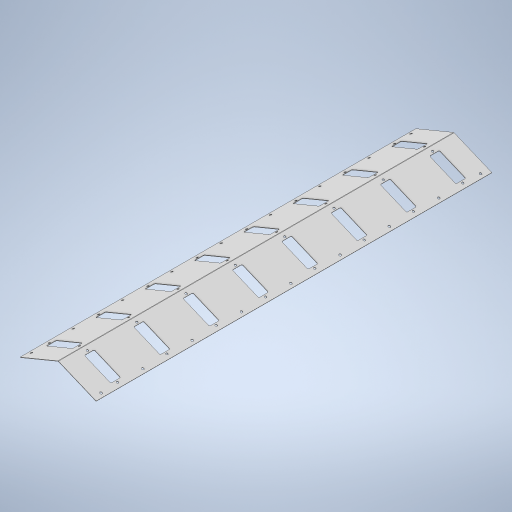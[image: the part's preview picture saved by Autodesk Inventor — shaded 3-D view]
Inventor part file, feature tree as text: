
AUTODESK INVENTOR PART (.ipt)
format: ipt  version: 2024.2 (Build 282272000, 272)  size: 656,896 bytes
history: native  units: mm
features: sketch x4, sheet_metal_op x3, extrude x3, other x3, pattern_linear x2, fillet x1, pattern_circular x1, mirror x1, chamfer x1
ambient origin geometry x8: Origin, YZ Plane, XZ Plane, XY Plane, X Axis, Y Axis, Z Axis, Center Point
bodies: Body1 (feature_tree)
feature tree (19):
  sheet_metal_op  "Contour Flange2"
  extrude  "Extrusion5"  Depth=0.9mm
  extrude  "Extrusion7"  Depth=2.0mm
  fillet  "Fillet2"  Radius=2.0mm
  pattern_circular  "Circular Pattern1"  [2 undecoded]
  pattern_linear  "Rectangular Pattern5"  Spacing1=2006.0mm  [1 undecoded]
  extrude  "Extrusion8"  Depth=2.0mm
  pattern_linear  "Rectangular Pattern6"  Spacing1=3.0mm  [1 undecoded]
  mirror  "Mirror5"
  other  "Corner Chamfer1"
  chamfer  "Corner Round1"
  sketch  "Sketch1"  dims[d46=506.0mm d47=0.9mm]
  other  "Plate4"
  sheet_metal_op  "Bend4"
  sheet_metal_op  "Corner4"
  sketch  "Sketch12"  dims[d48=4.0mm d49=2.0mm d50=2.0mm]
  sketch  "Sketch14"  dims[d51=1.0mm]
  sketch  "Sketch15"  dims[d52=4.0mm d53=2.0mm d54=2006.0mm d55=2.0mm d56=3.0mm d57=8.0mm d58=2.0mm d59=2.0mm d115=11.0mm d116=189.129mm d117=40.75mm d118=11.0mm d119=189.129mm d120=40.75mm d121=10.0mm d122=0.0mm d131=145.0mm d132=50.0mm d133=10.0mm d134=10.0mm d135=125.0mm d136=103.139mm d137=10.0mm d138=0.0mm d139=5.0mm d140=20.0mm d141=45.0deg d143=80.0mm d145=250.0mm d146=11.0mm d147=189.129mm d148=0.0mm d149=0.0mm d150=70.0mm d152=250.0mm d153=2.0mm d154=6.0mm d155=45.0deg d156=2.0mm]
  other  "Definition1"
note: 4 required parameter values undecoded (feature->parameter linkage not recoverable at this tier; creation-order binding heuristic only, values carry confidence <= 0.55)
